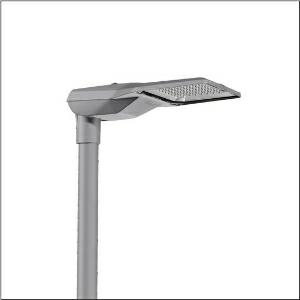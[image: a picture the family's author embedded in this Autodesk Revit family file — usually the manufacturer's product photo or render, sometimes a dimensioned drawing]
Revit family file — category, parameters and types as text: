
# Revit family: streetlight_sl_21_midi___pl52_5xe3h43s08lb_5466
name_source: partatom
category: Lighting Fixtures
units: mm (PartAtom-declared; Revit-internal decimal feet)

## family parameters
Cut with Voids When Loaded = No
Host = Face
Light Source = No
Part Type = Normal
Room Calculation Point = No
Round Connector Dimension = Use Diameter
Shared = No

## types (1)
- --- (1 x LED, 14690 lm, 99.6 W, 4000K)
    Apparent Load = 100 VA
    CIE Flux Codes = 27 59 98 100 100
    Color Rendering = 70
    Color Temperature = 4000K
    Default Elevation = 1800 mm
    Description = Streetlight SL 21 midi, mast luminaire, primary light control with lens, of PMMA, primary optical cover: cover, of toughened safety glass, transparent, light distribution: PL52, light emission: direct distribution, primary light characteristic: asymmetric, installation type: side-entry, post-top, LED, High Power LED, rated luminous flux: 14.690lm, luminous efficacy: 148lm/W, light colour: 740, colour temperature: 4000K, control gear: D4i, control: overheat protection, constant luminous flux control, time-dependent luminous flux control, flexible luminous flux parameterisation, pre-setting: logarithmic dimming characteristic, mains connection: 230..240V, AC, 50/60Hz, start of lifetime: 100W, end of service life: 102W, reduction: 46W, luminaire housing, of diecast aluminium, powder-coated, SITECO metallic grey (DB 702S), corrosivity category C5 high according to DIN EN ISO 12944, please order mast flange separately, inclination adjustable: 0°, 5°, 10°, 15°, sealing non-destructively replaceable, multi-level sealing system, length: 644mm, width: 335mm, height: 110mm, mast flange for spigot size: 42mm (side-entry): 5XC10008XM4, 60/48mm (side-entry/post-top): 5XC10108XM2, 76/60mm (side-entry/post-top): 5XC10108XM1, mounting height: 4..8m, Smart Interface above, protection rating (complete): IP66, insulation class (complete): insulation class II (safety insulation), certification: CE, ENEC, ENEC+, VDE, impact resistance: IK10, permissible operating ambient temperature for outdoor applications: -40..+50°C, standard-compliant lighting for roads and squares, packaging unit: 1 piece

Light Distribution: PL52
    Height = 111 mm
    Lamp = 1 x LED
    Lamp Light Flux = 14690 lm
    Lamp Power = 99.6 W
    Lamp count = 1
    Length = 644 mm
    Luminous efficacy = 147 lm/W
    Manufacturer = Siteco
    ModVariant = No
    Model = 5XE3H43S08LB
    Number of Poles = 1
    OnlyDefault = Yes
    Power Factor = 1
    Product Name = Streetlight SL 21 midi | PL52
    Product group = mast luminaire | pylon top
    ProductGroupID = 6100
    Protection Class = Protection class II
    Protection Degree = IP 66
    RLX_Detail_Level = 1
    RLX_Emergency_Light_Flux = 0 lm
    RLX_Emergency_Type = 0
    RLX_Emergency_Type_DB = No
    RlxData = <blob elided: 36429 chars, md5=a6fb2927>
    Socket = socket
    Standby Power = 0 W
    System Light Flux = 14690 lm
    System Power = 100 W
    Type Comments = factory setting: luminous flux: 100 % | dim-lin: 254 | 1020 mA
    Type Image = l_1004302.jpg
    URL = http://relux.com
    VarID = @adj_032109
    Voltage = 0 V
    Weight = 0.00 kg
    Width = 336 mm

## geometry (parser evidence)
native form markers: Blend x4, Sweep x8
no freeform markers — native parametric forms only
